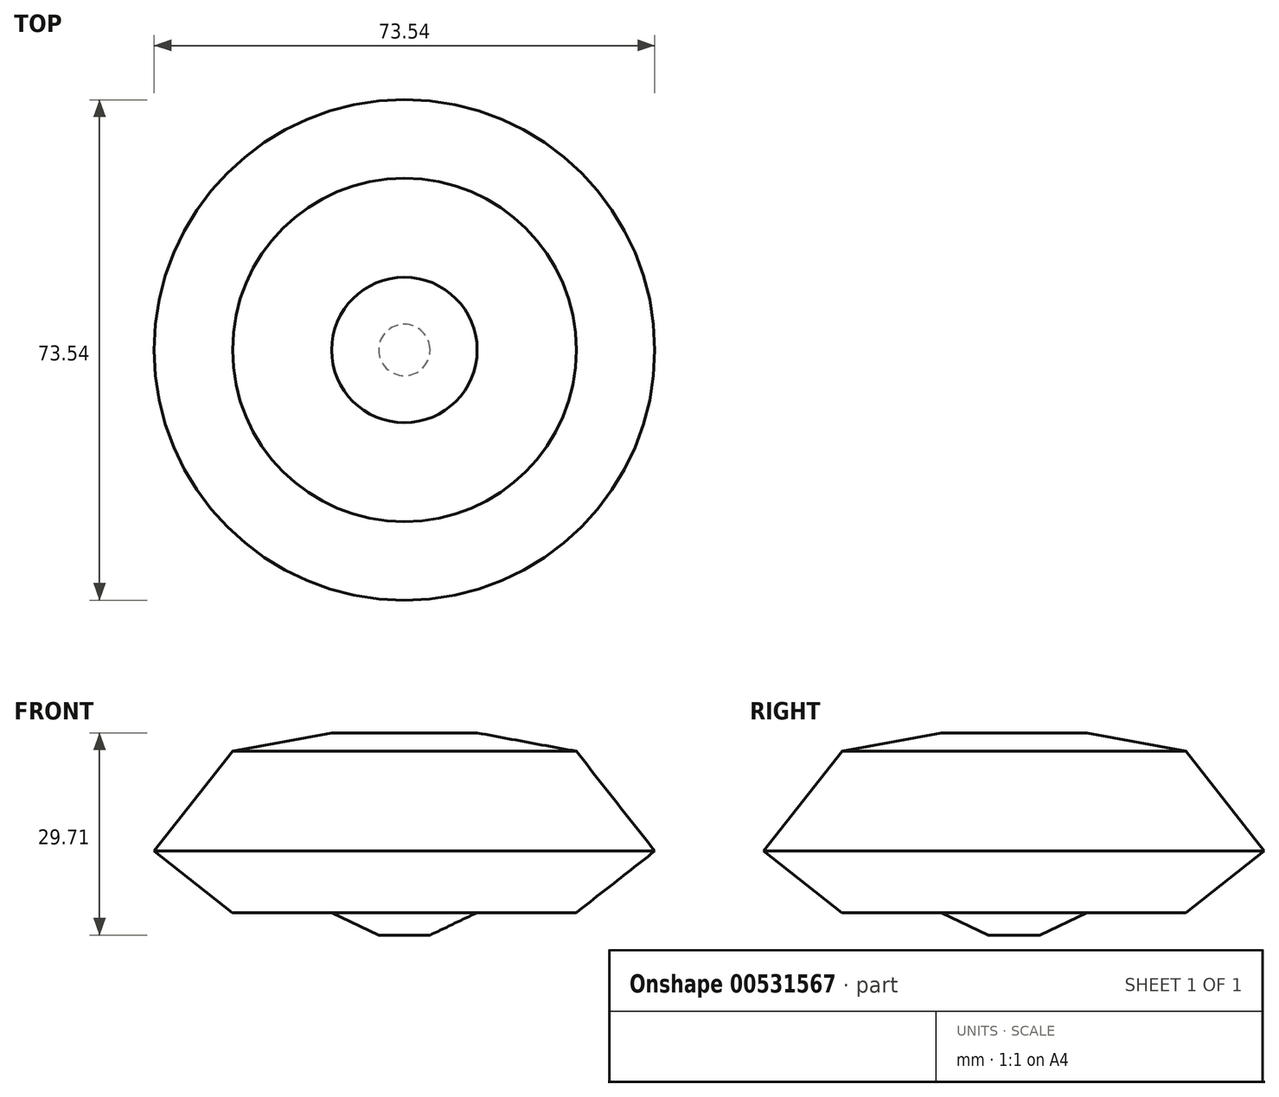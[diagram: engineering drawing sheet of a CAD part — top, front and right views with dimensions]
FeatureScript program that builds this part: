
annotation { "Feature Type Name" : "Feature", "Feature Type Description" : "" }
export const myFeature = defineFeature(function(context is Context, id is Id, definition is map)
    precondition{}
    {
        {
            var Q0;
            Q0=qCreatedBy(makeId("Front.planeOp"),FACE);
            var sketch = newSketch(context, id + "F0", { "sketchPlane" : qUnion([Q0])});
            skLineSegment(sketch, "E0", {"start": v(0, 0) * mm, "end": v(3.77, 0) * mm});
            skLineSegment(sketch, "E1", {"start": v(3.77, 0) * mm, "end": v(10.69, 3.3) * mm});
            skLineSegment(sketch, "E2", {"start": v(10.69, 3.3) * mm, "end": v(25.26, 3.3) * mm});
            skLineSegment(sketch, "E3", {"start": v(25.26, 3.3) * mm, "end": v(36.77, 12.34) * mm});
            skLineSegment(sketch, "E4", {"start": v(36.77, 12.34) * mm, "end": v(25.25, 27) * mm});
            skLineSegment(sketch, "E5", {"start": v(25.25, 27) * mm, "end": v(10.69, 29.7) * mm});
            skLineSegment(sketch, "E6", {"start": v(10.69, 29.7) * mm, "end": v(0, 29.7) * mm});
            skLineSegment(sketch, "E7", {"start": v(0, 29.7) * mm, "end": v(0, 0) * mm});
            skSolve(sketch);
        }
        {
            var Q0;
            Q0=makeQuery(id+"F0.imprint","IMPRINT",FACE,{"disambiguationData":[TD([[makeQuery(id+"F0.imprint","IMPRINT",EDGE,{"derivedFrom":sQuery(id+"F0.wireOp",EDGE,"E0")}),1.0]])]});
            var Q1;
            Q1=sQuery(id+"F0.wireOp",EDGE,"E7");
            revolve(context, id + "F1", {"entities" : qUnion([Q0]), "axis" : qUnion([Q1]), "revolveType" : RevolveType.FULL});
        }
    });
